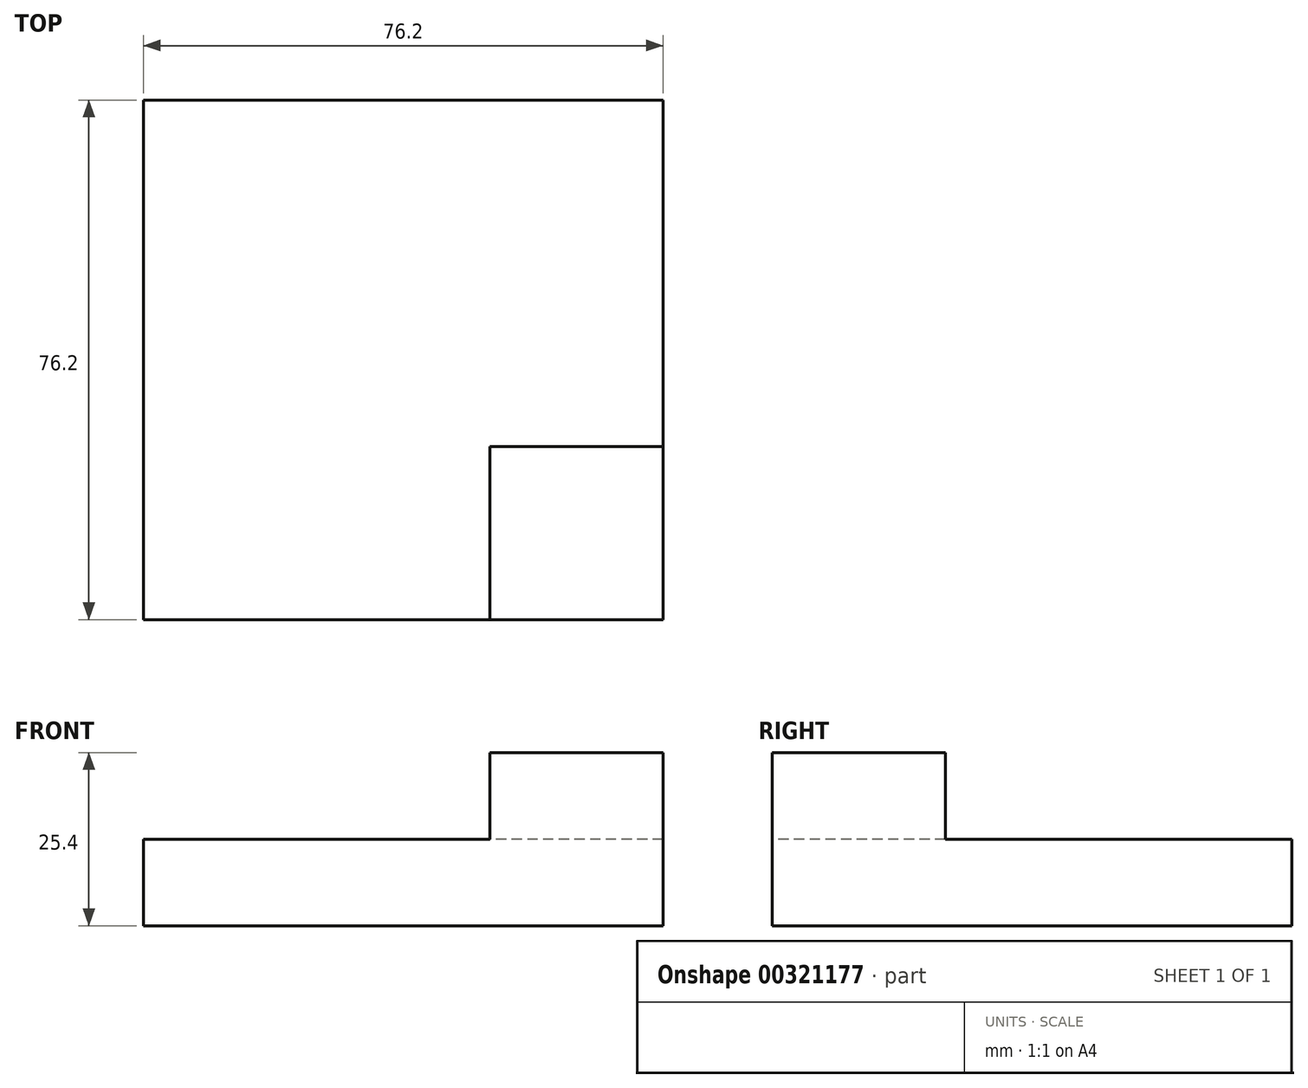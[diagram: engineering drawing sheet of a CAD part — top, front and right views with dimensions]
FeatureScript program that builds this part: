
annotation { "Feature Type Name" : "Feature", "Feature Type Description" : "" }
export const myFeature = defineFeature(function(context is Context, id is Id, definition is map)
    precondition{}
    {
        {
            var Q0;
            Q0=qCreatedBy(makeId("Top.planeOp"),FACE);
            var sketch = newSketch(context, id + "F0", { "sketchPlane" : qUnion([Q0])});
            skLineSegment(sketch, "E0", {"start": v(-37.14, -28.73) * mm, "end": v(39.06, -28.73) * mm});
            skLineSegment(sketch, "E1", {"start": v(39.06, -28.73) * mm, "end": v(39.06, 47.47) * mm});
            skLineSegment(sketch, "E2", {"start": v(39.06, 47.47) * mm, "end": v(-37.14, 47.47) * mm});
            skLineSegment(sketch, "E3", {"start": v(-37.14, 47.47) * mm, "end": v(-37.14, -28.73) * mm});
            skSolve(sketch);
        }
        {
            var Q0;
            Q0=makeQuery(id+"F0.imprint","IMPRINT",FACE,{"disambiguationData":[TD([[makeQuery(id+"F0.imprint","IMPRINT",EDGE,{"derivedFrom":sQuery(id+"F0.wireOp",EDGE,"E0")}),1.0]])]});
            extrude(context, id + "F1", {"entities" : qUnion([Q0]), "depth" : 12.7 * mm});
        }
        {
            var Q0;
            Q0=makeQuery(id+"F1.opExtrude","CAP_FACE",FACE,{"disambiguationData":[OSD([sQuery(id+"F0.wireOp",EDGE,"E0"),sQuery(id+"F0.wireOp",EDGE,"E1"),sQuery(id+"F0.wireOp",EDGE,"E2"),sQuery(id+"F0.wireOp",EDGE,"E3")])],"isStart":false});
            var sketch = newSketch(context, id + "F2", { "sketchPlane" : qUnion([Q0])});
            skLineSegment(sketch, "E4", {"start": v(-37.14, -3.33) * mm, "end": v(-11.74, -3.33) * mm});
            skLineSegment(sketch, "E5", {"start": v(-11.74, -3.33) * mm, "end": v(-11.74, -28.73) * mm});
            skLineSegment(sketch, "E6", {"start": v(39.06, -3.33) * mm, "end": v(13.66, -3.33) * mm});
            skLineSegment(sketch, "E7", {"start": v(13.66, -3.33) * mm, "end": v(13.66, -28.73) * mm});
            skLineSegment(sketch, "E8", {"start": v(13.66, 47.47) * mm, "end": v(13.66, 22.07) * mm});
            skLineSegment(sketch, "E9", {"start": v(13.66, 22.07) * mm, "end": v(39.06, 22.07) * mm});
            skLineSegment(sketch, "E10", {"start": v(-11.74, 47.47) * mm, "end": v(-11.74, 22.07) * mm});
            skLineSegment(sketch, "E11", {"start": v(-11.74, 22.07) * mm, "end": v(-37.14, 22.07) * mm});
            skSolve(sketch);
        }
        {
            var Q0;
            {var subQ0=sQuery(id+"F2.wireOp",EDGE,"E6");Q0=makeQuery(id+"F2.imprint","IMPRINT",FACE,{"disambiguationData":[TD([[makeQuery(id+"F2.imprint","IMPRINT",EDGE,{"derivedFrom":subQ0}),1.0]])]});}
            extrude(context, id + "F3", {"entities" : qUnion([Q0]), "operationType" : NewBodyOperationType.ADD, "depth" : 12.7 * mm});
        }
    });
